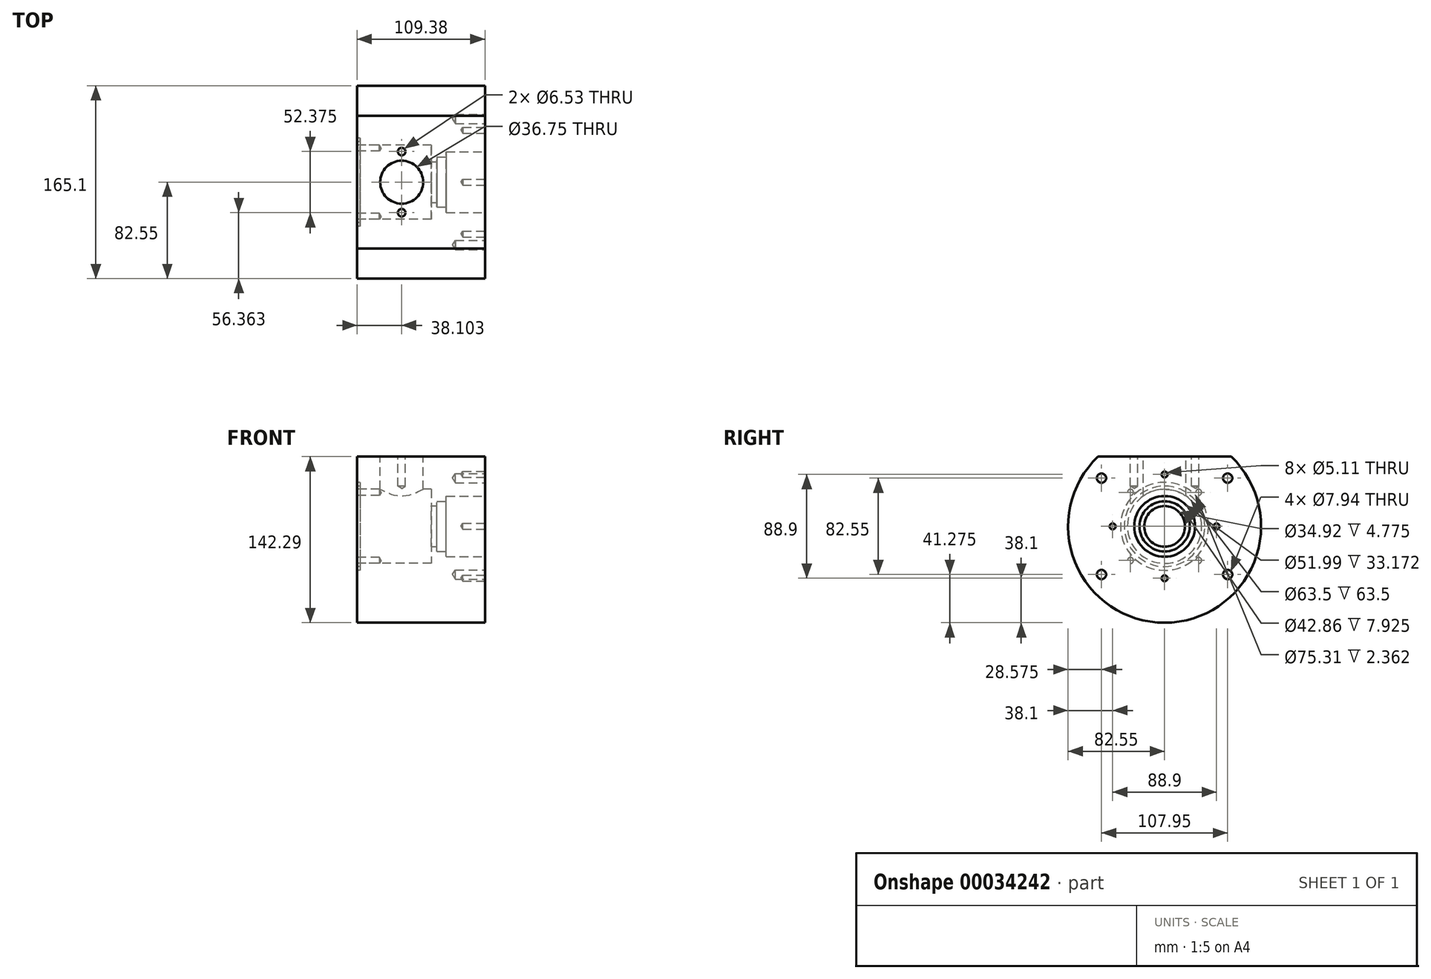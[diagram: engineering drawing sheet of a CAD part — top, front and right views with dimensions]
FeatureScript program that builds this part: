
annotation { "Feature Type Name" : "Feature", "Feature Type Description" : "" }
export const myFeature = defineFeature(function(context is Context, id is Id, definition is map)
    precondition{}
    {
        {
            var Q0;
            Q0=qCreatedBy(makeId("Right.planeOp"),FACE);
            var sketch = newSketch(context, id + "F0", { "sketchPlane" : qUnion([Q0])});
            skArc(sketch, "E0", {"start": v(-56.97, 59.74) * mm, "mid": v(0, -82.55) * mm, "end": v(56.97, 59.74) * mm});
            skLineSegment(sketch, "E1", {"start": v(-56.97, 59.74) * mm, "end": v(56.97, 59.74) * mm});
            skPoint(sketch, "E2.orphan", {"position": v(69.57, 59.74) * mm});
            skSolve(sketch);
        }
        {
            var Q0;
            Q0=makeQuery(id+"F0.imprint","IMPRINT",FACE,{"disambiguationData":[TD([[makeQuery(id+"F0.imprint","IMPRINT",EDGE,{"derivedFrom":sQuery(id+"F0.wireOp",EDGE,"E0")}),1.0]])]});
            extrude(context, id + "F1", {"entities" : qUnion([Q0]), "oppositeDirection" : true, "depth" : 106.2 * mm});
        }
        {
            var Q0;
            Q0=makeQuery(id+"F1.opExtrude","CAP_FACE",FACE,{"disambiguationData":[OSD([sQuery(id+"F0.wireOp",EDGE,"E0"),sQuery(id+"F0.wireOp",EDGE,"E1")])],"isStart":true});
            var sketch = newSketch(context, id + "F2", { "sketchPlane" : qUnion([Q0])});
            skCircle(sketch, "E3", {"center": v(0, 0) * mm, "radius": 26 * mm});
            skSolve(sketch);
        }
        {
            var Q0;
            Q0 = qSketchRegion(id + "F2", true);
            extrude(context, id + "F3", {"entities" : qUnion([Q0]), "operationType" : NewBodyOperationType.REMOVE, "oppositeDirection" : true, "depth" : 30 * mm});
        }
        {
            var Q0;
            Q0=makeQuery(id+"F1.opExtrude","CAP_FACE",FACE,{"disambiguationData":[OSD([sQuery(id+"F0.wireOp",EDGE,"E0"),sQuery(id+"F0.wireOp",EDGE,"E1")])],"isStart":false});
            var sketch = newSketch(context, id + "F4", { "sketchPlane" : qUnion([Q0])});
            skCircle(sketch, "E4", {"center": v(0, 0) * mm, "radius": 31.75 * mm});
            skSolve(sketch);
        }
        {
            var Q0;
            Q0 = qSketchRegion(id + "F4", true);
            extrude(context, id + "F5", {"entities" : qUnion([Q0]), "operationType" : NewBodyOperationType.REMOVE, "oppositeDirection" : true, "depth" : 63.5 * mm});
        }
        {
            var Q0;
            Q0=makeQuery(id+"F3.boolean.opBoolean","COPY",FACE,{"derivedFrom":makeQuery(id+"F3.opExtrude","CAP_FACE",FACE,{"disambiguationData":[OSD([sQuery(id+"F2.wireOp",EDGE,"E3")])],"isStart":false})});
            var sketch = newSketch(context, id + "F6", { "sketchPlane" : qUnion([Q0])});
            skCircle(sketch, "E5", {"center": v(0, 0) * mm, "radius": 17.46 * mm});
            skSolve(sketch);
        }
        {
            var Q0;
            Q0 = qSketchRegion(id + "F6", true);
            extrude(context, id + "F7", {"entities" : qUnion([Q0]), "operationType" : NewBodyOperationType.REMOVE, "endBound" : BoundingType.THROUGH_ALL, "oppositeDirection" : true, "depth" : 25.4 * mm});
        }
        {
            var Q0;
            Q0=makeQuery(id+"F3.boolean.opBoolean","COPY",FACE,{"derivedFrom":makeQuery(id+"F3.opExtrude","CAP_FACE",FACE,{"disambiguationData":[OSD([sQuery(id+"F2.wireOp",EDGE,"E3")])],"isStart":false})});
            var sketch = newSketch(context, id + "F8", { "sketchPlane" : qUnion([Q0])});
            skCircle(sketch, "E6", {"center": v(0, 0) * mm, "radius": 21.43 * mm});
            skSolve(sketch);
        }
        {
            var Q0;
            Q0=makeQuery(id+"F8.imprint","IMPRINT",FACE,{"disambiguationData":[TD([[makeQuery(id+"F8.imprint","IMPRINT",EDGE,{"derivedFrom":makeQuery(id+"F7.boolean.opBoolean","COPY",EDGE,{"derivedFrom":makeQuery(id+"F7.opExtrude","CAP_EDGE",EDGE,{"disambiguationData":[OSD([sQuery(id+"F6.wireOp",EDGE,"E5")])],"isStart":true})})}),1.0]])]});
            var Q1;
            Q1=makeQuery(id+"F8.imprint","IMPRINT",FACE,{"disambiguationData":[TD([[makeQuery(id+"F8.imprint","IMPRINT",EDGE,{"derivedFrom":sQuery(id+"F8.wireOp",EDGE,"E6")}),1.0]])]});
            extrude(context, id + "F9", {"entities" : qUnion([Q0, Q1]), "operationType" : NewBodyOperationType.REMOVE, "oppositeDirection" : true, "depth" : 7.92 * mm});
        }
        {
            var Q0;
            Q0=makeQuery(id+"F1.opExtrude","SWEPT_FACE",FACE,{"disambiguationData":[OSD([sQuery(id+"F0.wireOp",EDGE,"E1")])]});
            var sketch = newSketch(context, id + "F10", { "sketchPlane" : qUnion([Q0])});
            skCircle(sketch, "E7", {"center": v(-68.1, 0) * mm, "radius": 18.38 * mm});
            skPoint(sketch, "E7.centerSnap0", {"position": v(0, 0) * mm});
            skSolve(sketch);
        }
        {
            var Q0;
            Q0=makeQuery(id+"F10.imprint","IMPRINT",FACE,{"disambiguationData":[TD([[makeQuery(id+"F10.imprint","IMPRINT",EDGE,{"derivedFrom":sQuery(id+"F10.wireOp",EDGE,"E7")}),1.0]])]});
            extrude(context, id + "F11", {"entities" : qUnion([Q0]), "operationType" : NewBodyOperationType.REMOVE, "endBound" : BoundingType.UP_TO_NEXT, "oppositeDirection" : true, "depth" : 25.4 * mm});
        }
        {
            var Q0;
            Q0=makeQuery(id+"F1.opExtrude","CAP_FACE",FACE,{"disambiguationData":[OSD([sQuery(id+"F0.wireOp",EDGE,"E0"),sQuery(id+"F0.wireOp",EDGE,"E1")])],"isStart":true});
            extrude(context, id + "F12", {"entities" : qUnion([Q0]), "operationType" : NewBodyOperationType.ADD, "depth" : 3.17 * mm});
        }
        {
            var Q0;
            {var subQ0=sQuery(id+"F0.wireOp",EDGE,"E1");Q0=makeQuery(id+"F12.boolean.opBoolean","MERGE",FACE,{"derivedFrom":[makeQuery(id+"F1.opExtrude","SWEPT_FACE",FACE,{"disambiguationData":[OSD([subQ0])]}),makeQuery(id+"F12.opExtrude","SWEPT_FACE",FACE,{"disambiguationData":[OSD([subQ0])]})]});}
            var sketch = newSketch(context, id + "F13", { "sketchPlane" : qUnion([Q0])});
            skPoint(sketch, "E8", {"position": v(-68.1, 26.19) * mm});
            skPoint(sketch, "E9", {"position": v(-68.1, -26.19) * mm});
            skSolve(sketch);
        }
        {
            var Q0;
            Q0=sQuery(id+"F13.wireOp",VERTEX,"E8");
            var Q1;
            Q1=sQuery(id+"F13.wireOp",VERTEX,"E9");
            var Q2;
            Q2=makeQuery(id+"F1.opExtrude","SWEPT_BODY",BODY,{"disambiguationData":[OSD([sQuery(id+"F0.wireOp",EDGE,"E0"),sQuery(id+"F0.wireOp",EDGE,"E1")])]});
            hole(context, id + "F14", {"style" : HoleStyle.SIMPLE, "holeDiameter" : 6.53 * mm, "endStyle" : HoleEndStyle.BLIND, "holeDepth" : 25.4 * mm, "locations" : qUnion([Q0, Q1]), "scope" : qUnion([Q2])});
        }
        {
            var Q0;
            Q0=makeQuery(id+"F1.opExtrude","CAP_FACE",FACE,{"disambiguationData":[OSD([sQuery(id+"F0.wireOp",EDGE,"E0"),sQuery(id+"F0.wireOp",EDGE,"E1")])],"isStart":false});
            var sketch = newSketch(context, id + "F15", { "sketchPlane" : qUnion([Q0])});
            skPoint(sketch, "E10.center", {"position": v(0, 0) * mm});
            skPoint(sketch, "E11", {"position": v(29.19, -29.19) * mm});
            skPoint(sketch, "E12.1.0", {"position": v(29.19, 29.19) * mm});
            skPoint(sketch, "E12.2.0", {"position": v(-29.19, 29.19) * mm});
            skPoint(sketch, "E12.3.0", {"position": v(-29.19, -29.19) * mm});
            skSolve(sketch);
        }
        {
            var Q0;
            Q0=makeQuery(id+"F12.opExtrude","CAP_FACE",FACE,{"disambiguationData":[OSD([sQuery(id+"F0.wireOp",EDGE,"E0"),sQuery(id+"F0.wireOp",EDGE,"E1")])],"isStart":false});
            var sketch = newSketch(context, id + "F16", { "sketchPlane" : qUnion([Q0])});
            skPoint(sketch, "E13", {"position": v(44.45, 0) * mm});
            skPoint(sketch, "E14.1.0", {"position": v(0, 44.45) * mm});
            skPoint(sketch, "E14.2.0", {"position": v(-44.45, 0) * mm});
            skPoint(sketch, "E14.3.0", {"position": v(0, -44.45) * mm});
            skPoint(sketch, "E14.center", {"position": v(0, 0) * mm});
            skSolve(sketch);
        }
        {
            var Q0;
            Q0=sQuery(id+"F16.wireOp",VERTEX,"E13");
            var Q1;
            Q1=sQuery(id+"F16.wireOp",VERTEX,"E14.3.0");
            var Q2;
            Q2=sQuery(id+"F16.wireOp",VERTEX,"E14.2.0");
            var Q3;
            Q3=sQuery(id+"F16.wireOp",VERTEX,"E14.1.0");
            var Q4;
            Q4=makeQuery(id+"F1.opExtrude","SWEPT_BODY",BODY,{"disambiguationData":[OSD([sQuery(id+"F0.wireOp",EDGE,"E0"),sQuery(id+"F0.wireOp",EDGE,"E1")])]});
            hole(context, id + "F17", {"style" : HoleStyle.SIMPLE, "holeDiameter" : 5.1 * mm, "endStyle" : HoleEndStyle.BLIND, "holeDepth" : 19.05 * mm, "locations" : qUnion([Q0, Q1, Q2, Q3]), "scope" : qUnion([Q4])});
        }
        {
            var Q0;
            Q0=makeQuery(id+"F1.opExtrude","CAP_FACE",FACE,{"disambiguationData":[OSD([sQuery(id+"F0.wireOp",EDGE,"E0"),sQuery(id+"F0.wireOp",EDGE,"E1")])],"isStart":false});
            var sketch = newSketch(context, id + "F18", { "sketchPlane" : qUnion([Q0])});
            skCircle(sketch, "E15", {"center": v(0, 0) * mm, "radius": 37.66 * mm});
            skCircle(sketch, "E16", {"center": v(0, 0) * mm, "radius": 34.48 * mm});
            skSolve(sketch);
        }
        {
            var Q0;
            Q0=makeQuery(id+"F18.imprint","IMPRINT",FACE,{"disambiguationData":[TD([[makeQuery(id+"F18.imprint","IMPRINT",EDGE,{"derivedFrom":sQuery(id+"F18.wireOp",EDGE,"E15")}),1.0]])]});
            extrude(context, id + "F19", {"entities" : qUnion([Q0]), "operationType" : NewBodyOperationType.REMOVE, "oppositeDirection" : true, "depth" : 2.36 * mm});
        }
        {
            var Q0;
            Q0=sQuery(id+"F15.wireOp",VERTEX,"E12.2.0");
            var Q1;
            Q1=sQuery(id+"F15.wireOp",VERTEX,"E12.1.0");
            var Q2;
            Q2=sQuery(id+"F15.wireOp",VERTEX,"E11");
            var Q3;
            Q3=sQuery(id+"F15.wireOp",VERTEX,"E12.3.0");
            var Q4;
            Q4=makeQuery(id+"F1.opExtrude","SWEPT_BODY",BODY,{"disambiguationData":[OSD([sQuery(id+"F0.wireOp",EDGE,"E0"),sQuery(id+"F0.wireOp",EDGE,"E1")])]});
            hole(context, id + "F20", {"style" : HoleStyle.SIMPLE, "holeDiameter" : 5.1 * mm, "endStyle" : HoleEndStyle.BLIND, "holeDepth" : 19.05 * mm, "locations" : qUnion([Q0, Q1, Q2, Q3]), "scope" : qUnion([Q4])});
        }
        {
            var Q0;
            Q0=makeQuery(id+"F12.opExtrude","CAP_FACE",FACE,{"disambiguationData":[OSD([sQuery(id+"F0.wireOp",EDGE,"E0"),sQuery(id+"F0.wireOp",EDGE,"E1")])],"isStart":false});
            var sketch = newSketch(context, id + "F21", { "sketchPlane" : qUnion([Q0])});
            skCircle(sketch, "E17", {"center": v(53.98, 41.28) * mm, "radius": 3.97 * mm});
            skCircle(sketch, "E18", {"center": v(-53.98, 41.28) * mm, "radius": 3.97 * mm});
            skCircle(sketch, "E19.MirrorC", {"center": v(53.98, -41.28) * mm, "radius": 3.97 * mm});
            skCircle(sketch, "E20.MirrorC", {"center": v(-53.98, -41.28) * mm, "radius": 3.97 * mm});
            skSolve(sketch);
        }
        {
            var Q0;
            Q0=sQuery(id+"F21.wireOp",VERTEX,"E17.center");
            var Q1;
            Q1=sQuery(id+"F21.wireOp",VERTEX,"E18.center");
            var Q2;
            Q2=sQuery(id+"F21.wireOp",VERTEX,"E20.MirrorC.center");
            var Q3;
            Q3=sQuery(id+"F21.wireOp",VERTEX,"E19.MirrorC.center");
            var Q4;
            Q4=makeQuery(id+"F1.opExtrude","SWEPT_BODY",BODY,{"disambiguationData":[OSD([sQuery(id+"F0.wireOp",EDGE,"E0"),sQuery(id+"F0.wireOp",EDGE,"E1")])]});
            hole(context, id + "F22", {"style" : HoleStyle.SIMPLE, "holeDiameter" : 7.94 * mm, "endStyle" : HoleEndStyle.BLIND, "holeDepth" : 25.4 * mm, "locations" : qUnion([Q0, Q1, Q2, Q3]), "scope" : qUnion([Q4])});
        }
    });
